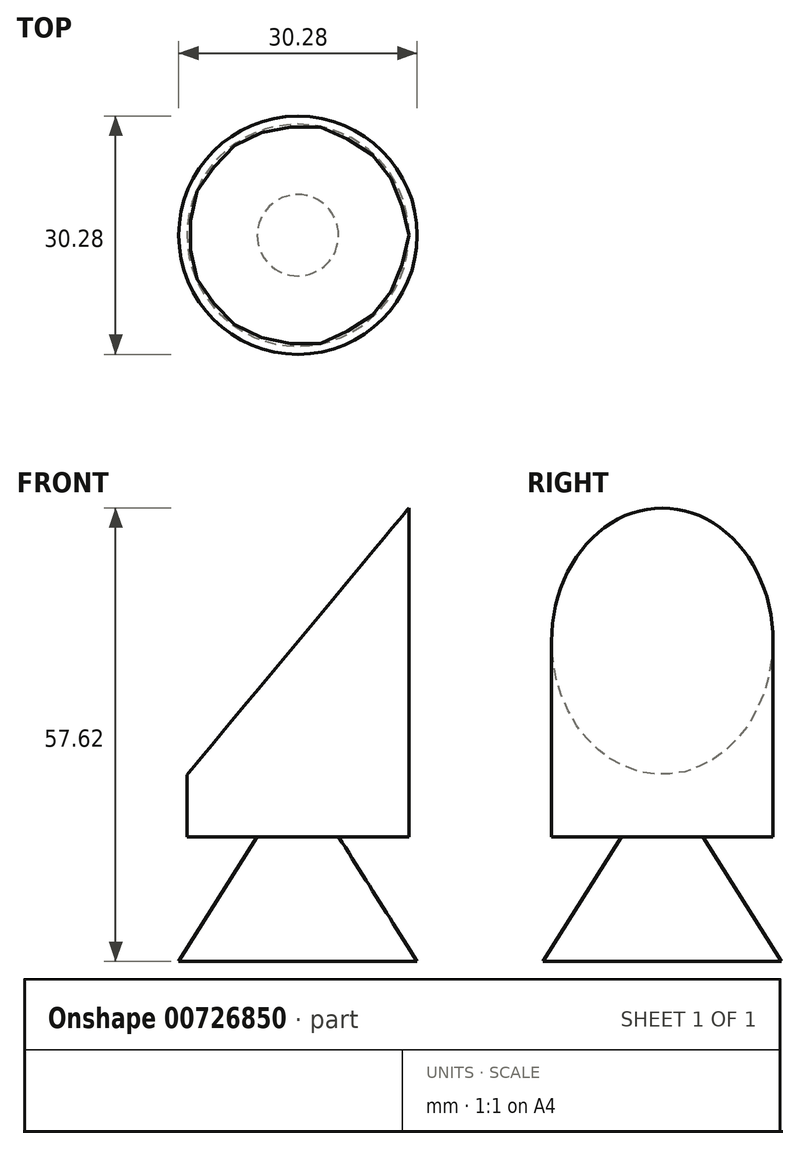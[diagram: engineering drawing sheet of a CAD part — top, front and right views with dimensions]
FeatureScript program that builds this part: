
annotation { "Feature Type Name" : "Feature", "Feature Type Description" : "" }
export const myFeature = defineFeature(function(context is Context, id is Id, definition is map)
    precondition{}
    {
        {
            var Q0;
            Q0=qCreatedBy(makeId("Front.planeOp"),FACE);
            var sketch = newSketch(context, id + "F0", { "sketchPlane" : qUnion([Q0])});
            skLineSegment(sketch, "E0", {"start": v(0, 0) * mm, "end": v(-15.14, 0) * mm});
            skLineSegment(sketch, "E1", {"start": v(-15.14, 0) * mm, "end": v(-5.16, 15.84) * mm});
            skLineSegment(sketch, "E2", {"start": v(-5.16, 15.84) * mm, "end": v(-14.09, 15.84) * mm});
            skLineSegment(sketch, "E3", {"start": v(-14.09, 15.84) * mm, "end": v(-14.09, 58.01) * mm});
            skLineSegment(sketch, "E4", {"start": v(-14.09, 58.01) * mm, "end": v(0, 58.01) * mm});
            skLineSegment(sketch, "E5", {"start": v(0, 58.01) * mm, "end": v(0, 0) * mm});
            skSolve(sketch);
        }
        {
            var Q0;
            Q0 = qSketchRegion(id + "F0", true);
            var Q1;
            Q1=sQuery(id+"F0.wireOp",EDGE,"E5");
            revolve(context, id + "F1", {"surfaceOperationType" : NewSurfaceOperationType.NEW, "entities" : qUnion([Q0]), "axis" : qUnion([Q1]), "revolveType" : RevolveType.FULL});
        }
        {
            var Q0;
            Q0=qCreatedBy(makeId("Front.planeOp"),FACE);
            var sketch = newSketch(context, id + "F2", { "sketchPlane" : qUnion([Q0])});
            skLineSegment(sketch, "E6", {"start": v(16.01, 59.94) * mm, "end": v(-20.04, 16.54) * mm});
            skLineSegment(sketch, "E7", {"start": v(-20.04, 16.54) * mm, "end": v(-20.04, 60.99) * mm});
            skLineSegment(sketch, "E8", {"start": v(-20.04, 60.99) * mm, "end": v(16.01, 59.94) * mm});
            skSolve(sketch);
        }
        {
            var Q0;
            Q0 = qSketchRegion(id + "F2", true);
            extrude(context, id + "F3", {"entities" : qUnion([Q0]), "operationType" : NewBodyOperationType.REMOVE, "endBound" : BoundingType.SYMMETRIC, "oppositeDirection" : true, "depth" : 34.8 * mm, "offsetDistance" : 25 * mm});
        }
    });
